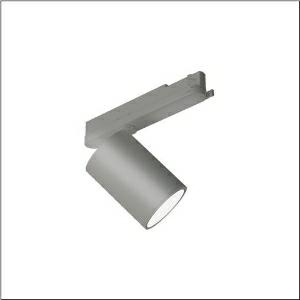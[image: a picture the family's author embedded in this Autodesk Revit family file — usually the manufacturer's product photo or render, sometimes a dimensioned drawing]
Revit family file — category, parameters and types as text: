
# Revit family: spot_31_51sf62mad4b
name_source: partatom
category: Lighting Fixtures
units: mm (PartAtom-declared; Revit-internal decimal feet)

## family parameters
Cut with Voids When Loaded = No
Host = Face
Light Source = No
Part Type = Normal
Room Calculation Point = No
Round Connector Dimension = Use Diameter
Shared = No

## types (1)
- --- (1 x LED, 5140 lm, 41.6 W, 4000K)
    Apparent Load = 42 VA
    CIE Flux Codes = 93 97 99 100 100
    Color Rendering = 90
    Color Temperature = 4000K
    Default Elevation = 1800 mm
    Description = Spot 31, directional spotlight, light control with lens, of PMMA, LED rated luminous flux: 4.930lm, light colour: 940, control gear: ECG Multilumen, with 3-phase adapter, mains connection: 220..240V, AC, 50/60Hz, of aluminium, metallic grey (RAL 9006), length: 213mm, diameter: 90mm, protection rating (complete): IP20, insulation class (complete): insulation class I (protective earthing), certification: CE, impact resistance: IK02, permissible ambient temperature for indoor applications: -20..+40°C, packaging unit: 1 piece
    Height = 175 mm
    Lamp = 1 x LED
    Lamp Light Flux = 5140 lm
    Lamp Power = 41.6 W
    Lamp count = 1
    Length = 90 mm
    Luminous efficacy = 124 lm/W
    Manufacturer = Siteco
    ModVariant = No
    Model = 51SF62MAD4B
    Mounting Place = Ceiling
    Mounting Type = Pendant
    Number of Poles = 1
    OnlyDefault = Yes
    Power Factor = 1
    Product Name = Spot 31
    Product group = directional spotlight
    ProductGroupID = 905
    Protection Class = Protection class I
    Protection Degree = IP 20
    RLX_Detail_Level = 1
    RLX_Emergency_Light_Flux = 0 lm
    RLX_Emergency_Type = 0
    RLX_Emergency_Type_DB = No
    RlxData = <blob elided: 20029 chars, md5=307973c1>
    Socket = socket
    Standby Power = 0 W
    System Light Flux = 5140 lm
    System Power = 42 W
    Type Comments = factory setting: luminous flux: 100 % | (ON | ON | ON | ON) | 1050 mA
    Type Image = l_1273725.jpg
    URL = http://relux.com
    VarID = @adj_146033
    Voltage = 0 V
    Weight = 0.00 kg
    Width = 0 mm  [stored 0 ft]

note: [stored X ft] marks values corroborated as IEEE doubles in the binary element streams (Revit-internal decimal feet)

## geometry (parser evidence)
native form markers: Blend x4, Sweep x10
no freeform markers — native parametric forms only
